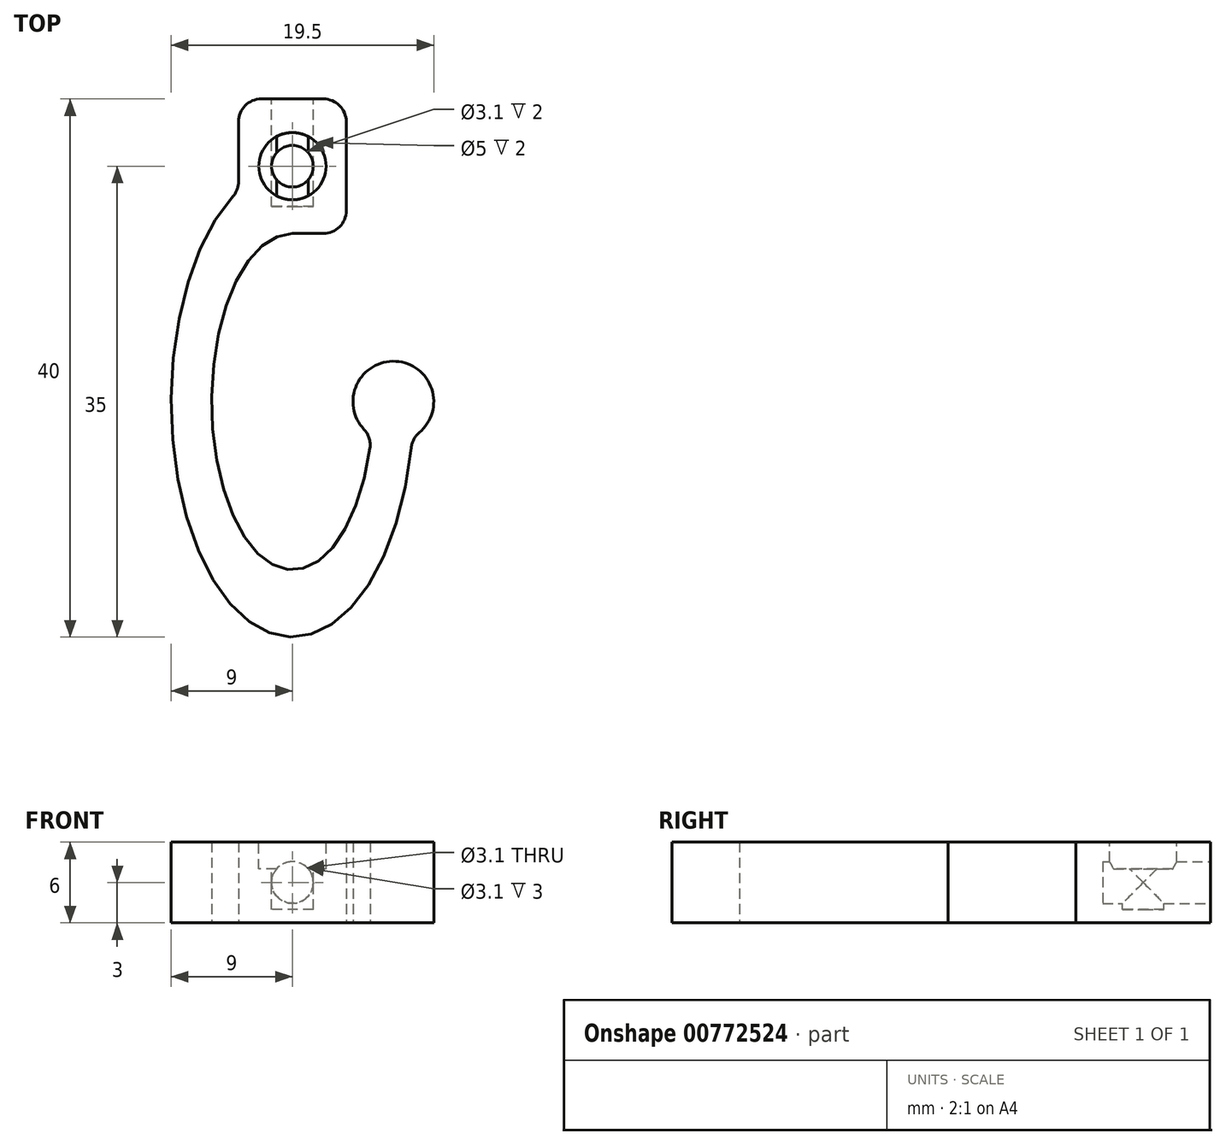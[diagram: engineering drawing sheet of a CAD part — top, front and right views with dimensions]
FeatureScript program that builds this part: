
annotation { "Feature Type Name" : "Feature", "Feature Type Description" : "" }
export const myFeature = defineFeature(function(context is Context, id is Id, definition is map)
    precondition{}
    {
        {
            var Q0;
            Q0=qCreatedBy(makeId("Top.planeOp"),FACE);
            var sketch = newSketch(context, id + "F0", { "sketchPlane" : qUnion([Q0])});
            skEllipticalArc(sketch, "E0", {});
            skLineSegment(sketch, "E1", {"start": v(0, 12.5) * mm, "end": v(0, 17.5) * mm, "construction": true});
            skLineSegment(sketch, "E2", {"start": v(0, 0) * mm, "end": v(6, 0) * mm, "construction": true});
            skLineSegment(sketch, "E3", {"start": v(-9, 0) * mm, "end": v(-6, 0) * mm, "construction": true});
            skLineSegment(sketch, "E4", {"start": v(9, 0) * mm, "end": v(-9, 0) * mm, "construction": true});
            skLineSegment(sketch, "E5", {"start": v(0, -17.5) * mm, "end": v(0, 17.5) * mm, "construction": true});
            skLineSegment(sketch, "E6", {"start": v(6, 0) * mm, "end": v(9, 0) * mm, "construction": true});
            skArc(sketch, "E7", {"start": v(8.9, -2.66) * mm, "mid": v(7.63, 3) * mm, "end": v(5.88, -2.52) * mm});
            skLineSegment(sketch, "E8.bottom", {"start": v(4, 12.5) * mm, "end": v(0, 12.5) * mm});
            skLineSegment(sketch, "E8.top", {"start": v(4, 22.5) * mm, "end": v(-4, 22.5) * mm});
            skLineSegment(sketch, "E8.left", {"start": v(4, 12.5) * mm, "end": v(4, 22.5) * mm});
            skLineSegment(sketch, "E8.right", {"start": v(-4, 15.68) * mm, "end": v(-4, 22.5) * mm});
            skPoint(sketch, "E8.middle", {"position": v(0, 17.5) * mm});
            skPoint(sketch, "E9.orphan", {"position": v(-4, 12.5) * mm});
            skEllipticalArc(sketch, "E10.trimOffspring", {});
            const initialGuessF0  = {"E0": [0, 0, 0, 1, 0.0125, 0.006, 0, 4.509171709937856], "E10.trimOffspring": [0, 0, 0, -1, 0.0175, 0.009, 3.6021466452711186, 1.4184636776947883]};
            skSetInitialGuess(sketch, initialGuessF0);
            skSolve(sketch);
        }
        {
            var Q0;
            Q0=makeQuery(id+"F0.imprint","IMPRINT",FACE,{"disambiguationData":[TD([[makeQuery(id+"F0.imprint","IMPRINT",EDGE,{"derivedFrom":sQuery(id+"F0.wireOp",EDGE,"E0")}),-1.0]])]});
            extrude(context, id + "F1", {"entities" : qUnion([Q0]), "depth" : 6 * mm, "offsetDistance" : 25 * mm});
        }
        {
            var Q0;
            Q0=makeQuery(id+"F1.opExtrude","SWEPT_EDGE",EDGE,{"disambiguationData":[OSD([sQuery(id+"F0.wireOp",EDGE,"E7"),sQuery(id+"F0.wireOp",EDGE,"E10.trimOffspring")])]});
            var Q1;
            Q1=makeQuery(id+"F1.opExtrude","SWEPT_EDGE",EDGE,{"disambiguationData":[OSD([sQuery(id+"F0.wireOp",EDGE,"E8.bottom"),sQuery(id+"F0.wireOp",EDGE,"E8.left")])]});
            var Q2;
            Q2=makeQuery(id+"F1.opExtrude","SWEPT_EDGE",EDGE,{"disambiguationData":[OSD([sQuery(id+"F0.wireOp",EDGE,"E0"),sQuery(id+"F0.wireOp",EDGE,"E7")])]});
            var Q3;
            Q3=makeQuery(id+"F1.opExtrude","SWEPT_EDGE",EDGE,{"disambiguationData":[OSD([sQuery(id+"F0.wireOp",EDGE,"E8.right"),sQuery(id+"F0.wireOp",EDGE,"E10.trimOffspring")])]});
            var Q4;
            Q4=makeQuery(id+"F1.opExtrude","SWEPT_EDGE",EDGE,{"disambiguationData":[OSD([sQuery(id+"F0.wireOp",EDGE,"E8.top"),sQuery(id+"F0.wireOp",EDGE,"E8.left")])]});
            var Q5;
            Q5=makeQuery(id+"F1.opExtrude","SWEPT_EDGE",EDGE,{"disambiguationData":[OSD([sQuery(id+"F0.wireOp",EDGE,"E8.top"),sQuery(id+"F0.wireOp",EDGE,"E8.right")])]});
            fillet(context, id + "F2", {"entities" : qUnion([Q0, Q1, Q2, Q3, Q4, Q5]), "radius" : 1.69 * mm, "tangentPropagation" : true, "allowEdgeOverflow" : false});
        }
        {
            var Q0;
            Q0=makeQuery(id+"F1.opExtrude","SWEPT_FACE",FACE,{"disambiguationData":[OSD([sQuery(id+"F0.wireOp",EDGE,"E8.top")])]});
            var sketch = newSketch(context, id + "F3", { "sketchPlane" : qUnion([Q0])});
            skLineSegment(sketch, "E11", {"start": v(0, 0) * mm, "end": v(0, 6) * mm, "construction": true});
            skLineSegment(sketch, "E12", {"start": v(-2.31, 3) * mm, "end": v(2.31, 3) * mm, "construction": true});
            skCircle(sketch, "E13", {"center": v(0, 3) * mm, "radius": 1.55 * mm});
            skSolve(sketch);
        }
        {
            var Q0;
            Q0=makeQuery(id+"F3.imprint","IMPRINT",FACE,{"disambiguationData":[TD([[makeQuery(id+"F3.imprint","IMPRINT",EDGE,{"derivedFrom":sQuery(id+"F3.wireOp",EDGE,"E13")}),1.0]])]});
            extrude(context, id + "F4", {"entities" : qUnion([Q0]), "operationType" : NewBodyOperationType.REMOVE, "oppositeDirection" : true, "depth" : 8 * mm, "offsetDistance" : 25 * mm});
        }
        {
            var Q0;
            Q0=makeQuery(id+"F1.opExtrude","CAP_FACE",FACE,{"disambiguationData":[OSD([sQuery(id+"F0.wireOp",EDGE,"E0"),sQuery(id+"F0.wireOp",EDGE,"E7"),sQuery(id+"F0.wireOp",EDGE,"E8.bottom"),sQuery(id+"F0.wireOp",EDGE,"E8.top"),sQuery(id+"F0.wireOp",EDGE,"E8.left"),sQuery(id+"F0.wireOp",EDGE,"E8.right"),sQuery(id+"F0.wireOp",EDGE,"E10.trimOffspring")])],"isStart":false});
            var sketch = newSketch(context, id + "F5", { "sketchPlane" : qUnion([Q0])});
            skLineSegment(sketch, "E14", {"start": v(0, 17.5) * mm, "end": v(-4, 17.5) * mm, "construction": true});
            skLineSegment(sketch, "E15", {"start": v(-4, 17.5) * mm, "end": v(0, 17.5) * mm, "construction": true});
            skLineSegment(sketch, "E16", {"start": v(0, 12.5) * mm, "end": v(0, 22.5) * mm, "construction": true});
            skCircle(sketch, "E17", {"center": v(0, 17.5) * mm, "radius": 1.55 * mm});
            skCircle(sketch, "E18", {"center": v(0, 17.5) * mm, "radius": 2.5 * mm});
            skSolve(sketch);
        }
        {
            var Q0;
            Q0=makeQuery(id+"F5.imprint","IMPRINT",FACE,{"disambiguationData":[TD([[makeQuery(id+"F5.imprint","IMPRINT",EDGE,{"derivedFrom":sQuery(id+"F5.wireOp",EDGE,"E17")}),1.0]])]});
            extrude(context, id + "F6", {"entities" : qUnion([Q0]), "operationType" : NewBodyOperationType.REMOVE, "oppositeDirection" : true, "depth" : 5 * mm, "offsetDistance" : 25 * mm});
        }
        {
            var Q0;
            Q0=qSketchRegion(id+"F5",true);
            extrude(context, id + "F7", {"entities" : qUnion([Q0]), "operationType" : NewBodyOperationType.REMOVE, "oppositeDirection" : true, "depth" : 2 * mm, "offsetDistance" : 25 * mm});
        }
    });
